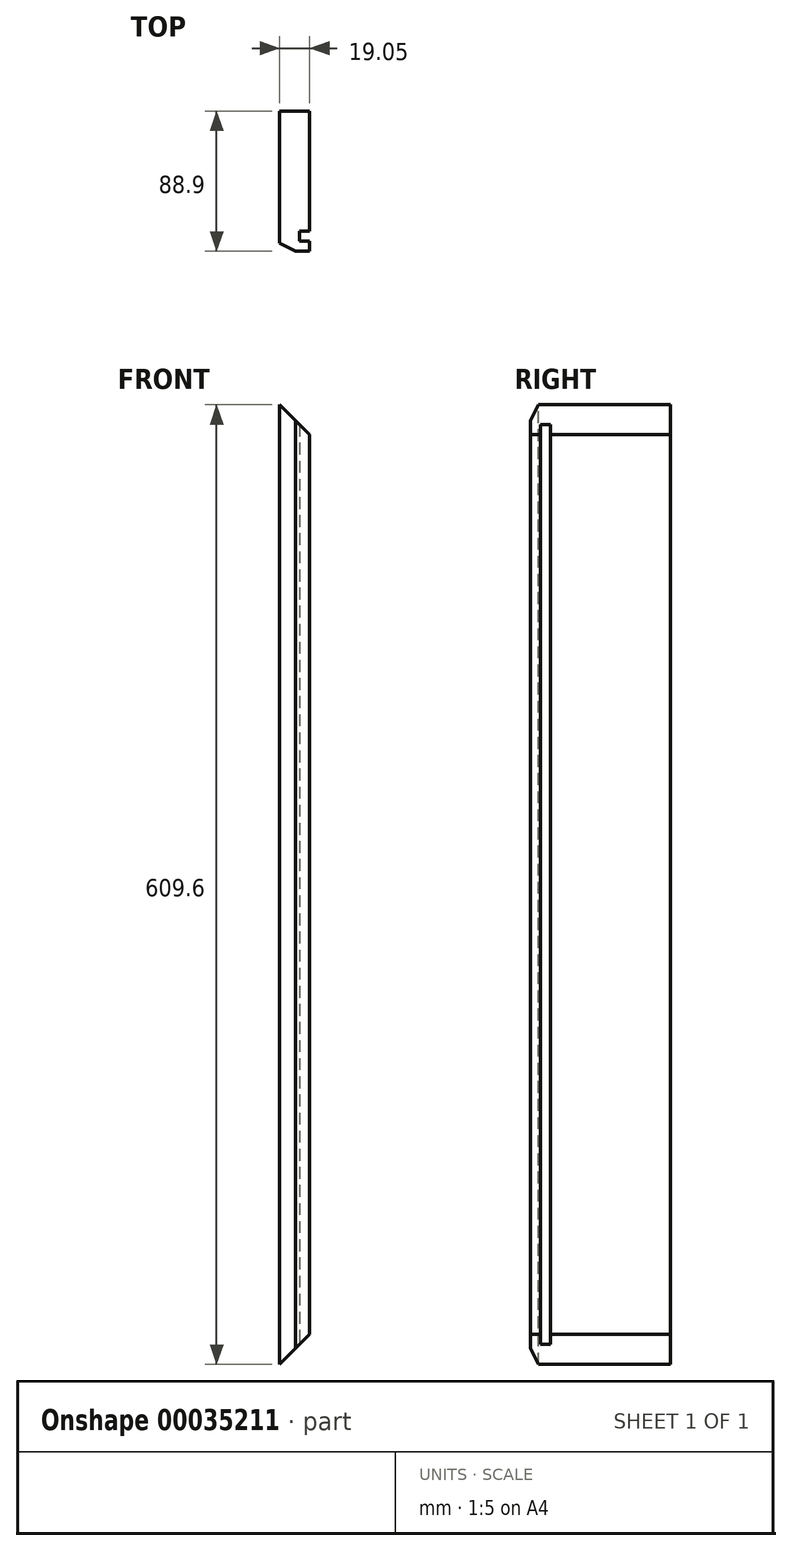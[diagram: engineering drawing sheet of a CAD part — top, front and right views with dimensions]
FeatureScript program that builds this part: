
annotation { "Feature Type Name" : "Feature", "Feature Type Description" : "" }
export const myFeature = defineFeature(function(context is Context, id is Id, definition is map)
    precondition{}
    {
        {
            var Q0;
            Q0=qCreatedBy(makeId("Right.planeOp"),FACE);
            var sketch = newSketch(context, id + "F0", { "sketchPlane" : qUnion([Q0])});
            skLineSegment(sketch, "E0.bottom", {"start": v(0, 0) * mm, "end": v(88.9, 0) * mm});
            skLineSegment(sketch, "E0.top", {"start": v(0, 609.6) * mm, "end": v(88.9, 609.6) * mm});
            skLineSegment(sketch, "E0.left", {"start": v(0, 0) * mm, "end": v(0, 609.6) * mm});
            skLineSegment(sketch, "E0.right", {"start": v(88.9, 0) * mm, "end": v(88.9, 609.6) * mm});
            skSolve(sketch);
        }
        {
            var Q0;
            Q0=makeQuery(id+"F0.imprint","IMPRINT",FACE,{"disambiguationData":[TD([[makeQuery(id+"F0.imprint","IMPRINT",EDGE,{"derivedFrom":sQuery(id+"F0.wireOp",EDGE,"E0.bottom")}),1.0]])]});
            extrude(context, id + "F1", {"entities" : qUnion([Q0]), "depth" : 19.05 * mm});
        }
        {
            var Q0;
            Q0=makeQuery(id+"F1.opExtrude","CAP_FACE",FACE,{"disambiguationData":[OSD([sQuery(id+"F0.wireOp",EDGE,"E0.bottom"),sQuery(id+"F0.wireOp",EDGE,"E0.top"),sQuery(id+"F0.wireOp",EDGE,"E0.left"),sQuery(id+"F0.wireOp",EDGE,"E0.right")])],"isStart":false});
            var sketch = newSketch(context, id + "F2", { "sketchPlane" : qUnion([Q0])});
            skLineSegment(sketch, "E1.bottom", {"start": v(6.35, 609.6) * mm, "end": v(12.7, 609.6) * mm});
            skLineSegment(sketch, "E1.top", {"start": v(6.35, 0) * mm, "end": v(12.7, 0) * mm});
            skLineSegment(sketch, "E1.left", {"start": v(6.35, 609.6) * mm, "end": v(6.35, 0) * mm});
            skLineSegment(sketch, "E1.right", {"start": v(12.7, 609.6) * mm, "end": v(12.7, 0) * mm});
            skSolve(sketch);
        }
        {
            var Q0;
            Q0=qSketchRegion(id+"F2",true);
            extrude(context, id + "F3", {"entities" : qUnion([Q0]), "operationType" : NewBodyOperationType.REMOVE, "oppositeDirection" : true, "depth" : 6.35 * mm});
        }
        {
            var Q0;
            Q0=makeQuery(id+"F1.opExtrude","CAP_EDGE",EDGE,{"disambiguationData":[OSD([sQuery(id+"F0.wireOp",EDGE,"E0.left")])],"isStart":true});
            chamfer(context, id + "F4", {"entities" : qUnion([Q0]), "chamferType" : ChamferType.TWO_OFFSETS, "width1" : 10.16 * mm, "oppositeDirection" : true, "width2" : 5.08 * mm, "tangentPropagation" : true});
        }
        {
            var Q0;
            Q0=makeQuery(id+"F1.opExtrude","SWEPT_FACE",FACE,{"disambiguationData":[OSD([sQuery(id+"F0.wireOp",EDGE,"E0.right")])]});
            var sketch = newSketch(context, id + "F5", { "sketchPlane" : qUnion([Q0])});
            skLineSegment(sketch, "E2", {"start": v(0, 609.6) * mm, "end": v(-19.05, 590.55) * mm});
            skLineSegment(sketch, "E3", {"start": v(-19.05, 590.55) * mm, "end": v(-19.05, 609.6) * mm});
            skLineSegment(sketch, "E4", {"start": v(-19.05, 609.6) * mm, "end": v(0, 609.6) * mm});
            skLineSegment(sketch, "E5", {"start": v(0, 0) * mm, "end": v(-19.05, 19.05) * mm});
            skLineSegment(sketch, "E6", {"start": v(-19.05, 19.05) * mm, "end": v(-19.05, 0) * mm});
            skLineSegment(sketch, "E7", {"start": v(-19.05, 0) * mm, "end": v(0, 0) * mm});
            skSolve(sketch);
        }
        {
            var Q0;
            Q0 = qSketchRegion(id + "F5", true);
            extrude(context, id + "F6", {"entities" : qUnion([Q0]), "operationType" : NewBodyOperationType.REMOVE, "endBound" : BoundingType.THROUGH_ALL, "oppositeDirection" : true, "depth" : 25.4 * mm});
        }
    });
